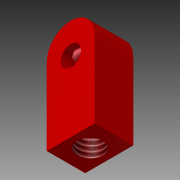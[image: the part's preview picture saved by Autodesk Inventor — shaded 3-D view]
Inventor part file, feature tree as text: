
AUTODESK INVENTOR PART (.ipt)
format: ipt  version: 2012 SP1 (Build 160190100, 190)  size: 105,984 bytes
history: native  units: in
note: dims shown in document units (in); Inventor stores cm internally (conversion verified against a paired STEP export)
features: sketch x3, extrude x2, hole x1
ambient origin geometry x8: Origin, YZ Plane, XZ Plane, XY Plane, X Axis, Y Axis, Z Axis, Center Point
bodies: Solid1 (feature_tree)
feature tree (6):
  extrude  "Extrusion1"  Depth=0.4724in
  hole  "Hole1"  [1 undecoded]
  extrude  "Extrusion2"  Depth=0.1476in
  sketch  "Sketch1"  dims[d0=0.2953in d1=0.4724in]
  sketch  "Sketch2"  dims[d2=0.2362in d3=0.0in d4=0.2953in]
  sketch  "Sketch3"  dims[d5=0.2362in d6=0.1476in d7=0.1181in d8=0.156in d9=0.175in d10=0.1575in d11=0.0787in d12=90.0deg d13=0.4921in d14=0.8108in d15=0.125in d16=0.0394in d17=0.0787in d18=0.0in d19=0.0394in d20=0.0394in]
note: 1 required parameter value undecoded (feature->parameter linkage not recoverable at this tier; creation-order binding heuristic only, values carry confidence <= 0.55)
